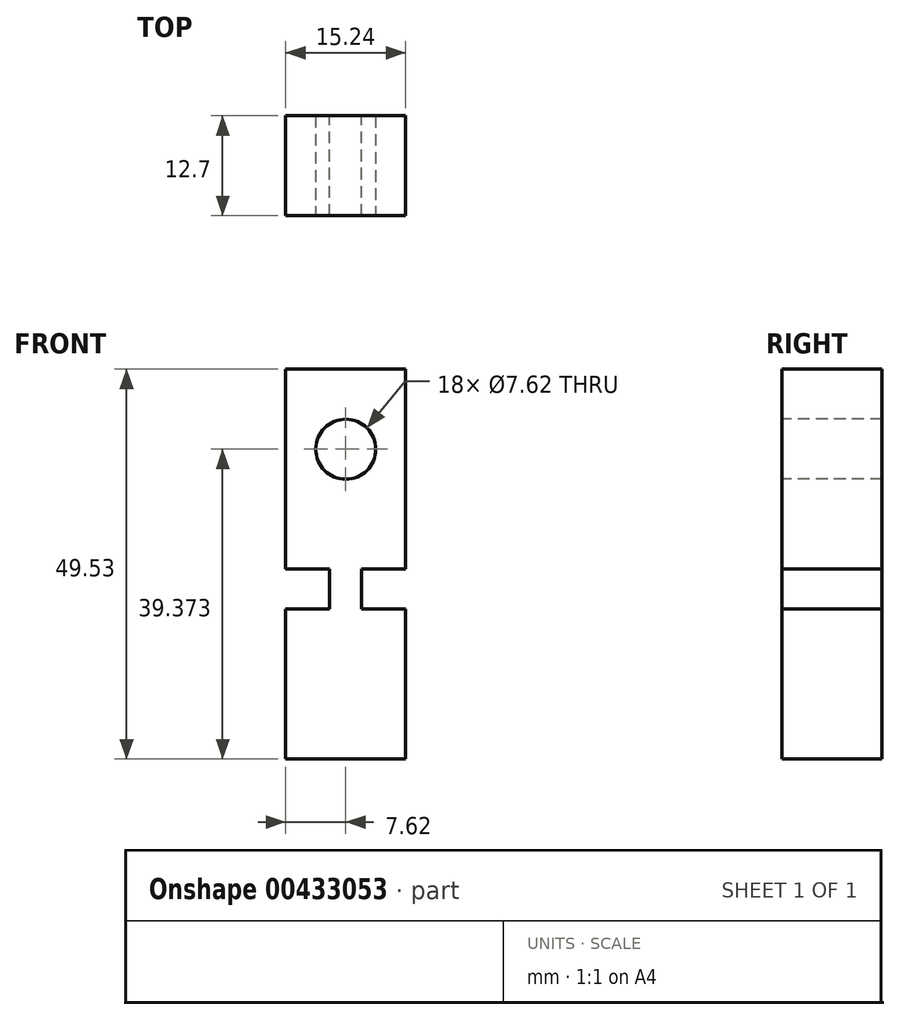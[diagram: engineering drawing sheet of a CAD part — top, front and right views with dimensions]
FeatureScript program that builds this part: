
annotation { "Feature Type Name" : "Feature", "Feature Type Description" : "" }
export const myFeature = defineFeature(function(context is Context, id is Id, definition is map)
    precondition{}
    {
        {
            var Q0;
            Q0=qCreatedBy(makeId("Front.planeOp"),FACE);
            var sketch = newSketch(context, id + "F0", { "sketchPlane" : qUnion([Q0])});
            skLineSegment(sketch, "E0", {"start": v(0, -8.09) * mm, "end": v(-7.62, -8.09) * mm});
            skLineSegment(sketch, "E1", {"start": v(-7.62, -8.09) * mm, "end": v(-7.62, 10.96) * mm});
            skLineSegment(sketch, "E2", {"start": v(-7.62, 10.96) * mm, "end": v(3.56, 10.96) * mm});
            skLineSegment(sketch, "E3", {"start": v(3.56, 16.04) * mm, "end": v(-7.62, 16.04) * mm});
            skLineSegment(sketch, "E4", {"start": v(-7.62, 16.04) * mm, "end": v(-7.62, 41.44) * mm});
            skLineSegment(sketch, "E5", {"start": v(-7.62, 41.44) * mm, "end": v(0, 41.44) * mm});
            skLineSegment(sketch, "E6.MirrorCS", {"start": v(7.62, 41.44) * mm, "end": v(0, 41.44) * mm});
            skLineSegment(sketch, "E7.MirrorCS", {"start": v(7.62, 16.04) * mm, "end": v(7.62, 41.44) * mm});
            skLineSegment(sketch, "E8.MirrorCS", {"start": v(-3.56, 16.04) * mm, "end": v(7.62, 16.04) * mm});
            skLineSegment(sketch, "E9.MirrorCS", {"start": v(7.62, 10.96) * mm, "end": v(-3.56, 10.96) * mm});
            skLineSegment(sketch, "E10.MirrorCS", {"start": v(7.62, -8.09) * mm, "end": v(7.62, 10.96) * mm});
            skLineSegment(sketch, "E11.MirrorCS", {"start": v(0, -8.09) * mm, "end": v(7.62, -8.09) * mm});
            skLineSegment(sketch, "E12", {"start": v(-2.03, 10.96) * mm, "end": v(-2.03, 16.04) * mm});
            skPoint(sketch, "E13.MirrorCS.end.orphan", {"position": v(-3.56, 16.04) * mm});
            skPoint(sketch, "E13.MirrorCS.start.orphan", {"position": v(-3.56, 10.96) * mm});
            skLineSegment(sketch, "E14.MirrorCS", {"start": v(2.03, 10.96) * mm, "end": v(2.03, 16.04) * mm});
            skSolve(sketch);
        }
        {
            var Q0;
            Q0=makeQuery(id+"F0.imprint","IMPRINT",FACE,{"disambiguationData":[TD([[makeQuery(id+"F0.imprint","IMPRINT",EDGE,{"derivedFrom":sQuery(id+"F0.wireOp",EDGE,"E0")}),-1.0]])]});
            var Q1;
            {var subQ0=sQuery(id+"F0.wireOp",EDGE,"E12");Q1=makeQuery(id+"F0.imprint","IMPRINT",FACE,{"disambiguationData":[TD([[makeQuery(id+"F0.imprint","IMPRINT",EDGE,{"derivedFrom":subQ0}),-1.0]])]});}
            var Q2;
            {var subQ0=sQuery(id+"F0.wireOp",EDGE,"E3");Q2=makeQuery(id+"F0.imprint","IMPRINT",FACE,{"disambiguationData":[TD([[makeQuery(id+"F0.imprint","IMPRINT",EDGE,{"derivedFrom":subQ0}),-1.0]])]});}
            extrude(context, id + "F1", {"entities" : qUnion([Q0, Q1, Q2]), "depth" : 12.7 * mm});
        }
        {
            var Q0;
            Q0=makeQuery(id+"F1.opExtrude","CAP_FACE",FACE,{"disambiguationData":[OSD([sQuery(id+"F0.wireOp",EDGE,"E0"),sQuery(id+"F0.wireOp",EDGE,"E1"),sQuery(id+"F0.wireOp",EDGE,"E2"),sQuery(id+"F0.wireOp",EDGE,"E3"),sQuery(id+"F0.wireOp",EDGE,"E4"),sQuery(id+"F0.wireOp",EDGE,"E5"),sQuery(id+"F0.wireOp",EDGE,"E6.MirrorCS"),sQuery(id+"F0.wireOp",EDGE,"E7.MirrorCS"),sQuery(id+"F0.wireOp",EDGE,"E8.MirrorCS"),sQuery(id+"F0.wireOp",EDGE,"E9.MirrorCS"),sQuery(id+"F0.wireOp",EDGE,"E10.MirrorCS"),sQuery(id+"F0.wireOp",EDGE,"E11.MirrorCS"),sQuery(id+"F0.wireOp",EDGE,"E12"),sQuery(id+"F0.wireOp",EDGE,"E14.MirrorCS")])],"isStart":false});
            var sketch = newSketch(context, id + "F2", { "sketchPlane" : qUnion([Q0])});
            skCircle(sketch, "E15", {"center": v(0, 31.28) * mm, "radius": 3.81 * mm});
            skSolve(sketch);
        }
        {
            var Q0;
            Q0=makeQuery(id+"F2.imprint","IMPRINT",FACE,{"disambiguationData":[TD([[makeQuery(id+"F2.imprint","IMPRINT",EDGE,{"derivedFrom":sQuery(id+"F2.wireOp",EDGE,"E15")}),1.0]])]});
            extrude(context, id + "F3", {"entities" : qUnion([Q0]), "operationType" : NewBodyOperationType.REMOVE, "oppositeDirection" : true, "depth" : 25.4 * mm});
        }
    });
